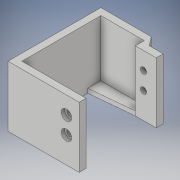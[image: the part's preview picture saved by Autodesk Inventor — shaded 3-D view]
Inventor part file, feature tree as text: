
AUTODESK INVENTOR PART (.ipt)
format: ipt  version: 2019 (Build 230136000, 136)  size: 154,112 bytes
history: native  units: mm
features: sketch x4, extrude x2, hole x2
ambient origin geometry x8: Origin, YZ Plane, XZ Plane, XY Plane, X Axis, Y Axis, Z Axis, Center Point
bodies: Body1 (feature_tree)
feature tree (8):
  extrude  "Extrusion10"  Depth=25.0mm
  extrude  "Extrusion12"  Depth=12.0mm
  hole  "Hole4"  [1 undecoded]
  hole  "Hole5"  [1 undecoded]
  sketch  "Sketch14"  dims[d59=45.5mm d60=25.0mm]
  sketch  "Sketch17"  dims[d61=5.1mm d62=12.0mm]
  sketch  "Sketch18"  dims[d64=4.0mm d65=4.0mm]
  sketch  "Sketch19"  dims[d66=4.0mm d67=4.0mm d68=8.0mm d69=35.0mm d70=0.0mm d75=2.5mm d76=0.0mm d77=29.7mm d78=20.0mm d79=3.5mm d80=6.0mm d81=6.0mm d82=7.0mm d83=90.0deg d84=6.5mm d85=0.0mm d86=3.5mm d87=6.0mm d88=6.0mm d89=2.0mm d90=90.0deg d91=6.5mm d92=0.0mm]
note: 2 required parameter values undecoded (feature->parameter linkage not recoverable at this tier; creation-order binding heuristic only, values carry confidence <= 0.55)
